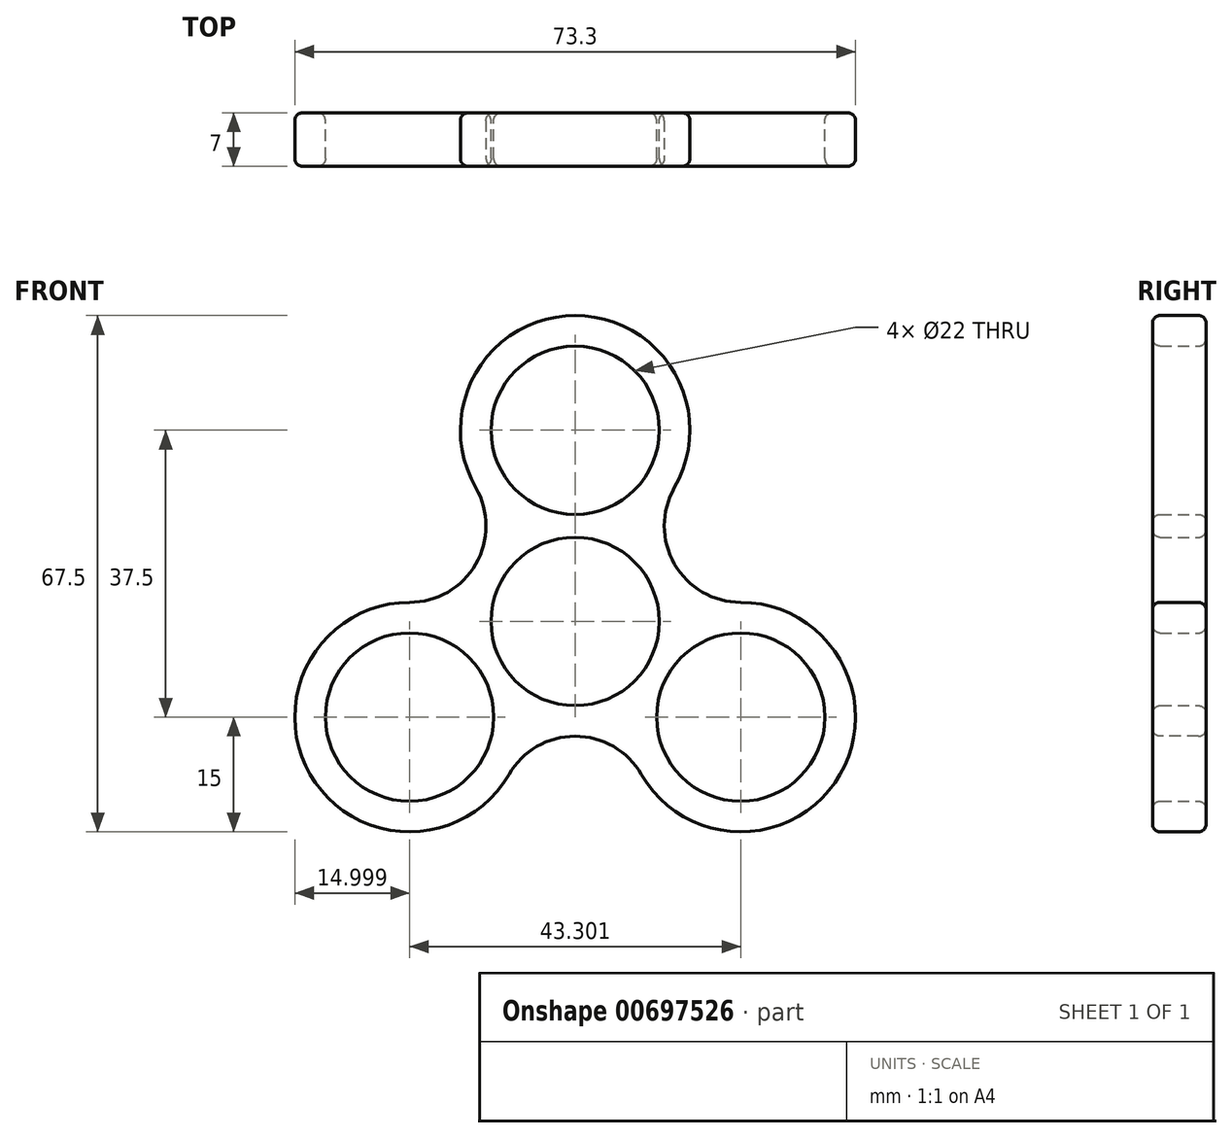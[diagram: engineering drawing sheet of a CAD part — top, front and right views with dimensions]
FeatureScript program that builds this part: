
annotation { "Feature Type Name" : "Feature", "Feature Type Description" : "" }
export const myFeature = defineFeature(function(context is Context, id is Id, definition is map)
    precondition{}
    {
        {
            var Q0;
            Q0=qCreatedBy(makeId("Front.planeOp"),FACE);
            var sketch = newSketch(context, id + "F0", { "sketchPlane" : qUnion([Q0])});
            skCircle(sketch, "E0", {"center": v(0, 0) * mm, "radius": 11 * mm});
            skArc(sketch, "E1", {"start": v(-8.3, 12.5) * mm, "mid": v(-13, 7.5) * mm, "end": v(-14.97, 0.93) * mm});
            skCircle(sketch, "E2", {"center": v(0, 0) * mm, "radius": 36.86 * mm, "construction": true});
            skLineSegment(sketch, "E3", {"start": v(0, 0) * mm, "end": v(31.92, -18.43) * mm, "construction": true});
            skLineSegment(sketch, "E4", {"start": v(0, 0) * mm, "end": v(0, 36.86) * mm, "construction": true});
            skLineSegment(sketch, "E5", {"start": v(0, 0) * mm, "end": v(-31.92, -18.43) * mm, "construction": true});
            skLineSegment(sketch, "E6", {"start": v(0, 0) * mm, "end": v(-13, -7.5) * mm});
            skLineSegment(sketch, "E7", {"start": v(0, 0) * mm, "end": v(-21.65, -12.5) * mm, "construction": true});
            skCircle(sketch, "E8", {"center": v(-21.65, -12.5) * mm, "radius": 11 * mm});
            skArc(sketch, "E9", {"start": v(-14.97, 0.93) * mm, "mid": v(-34.64, -20) * mm, "end": v(-6.68, -13.43) * mm});
            skLineSegment(sketch, "E10", {"start": v(0, 0) * mm, "end": v(0, 25) * mm, "construction": true});
            skCircle(sketch, "E11", {"center": v(0, 25) * mm, "radius": 11 * mm});
            skArc(sketch, "E12", {"start": v(8.3, 12.5) * mm, "mid": v(0, 40) * mm, "end": v(-8.3, 12.5) * mm});
            skLineSegment(sketch, "E13", {"start": v(0, 0) * mm, "end": v(21.65, -12.5) * mm, "construction": true});
            skCircle(sketch, "E14", {"center": v(21.65, -12.5) * mm, "radius": 11 * mm});
            skArc(sketch, "E15", {"start": v(6.68, -13.43) * mm, "mid": v(34.64, -20) * mm, "end": v(14.97, 0.93) * mm});
            skArc(sketch, "E16.trimOffspring", {"start": v(14.97, 0.93) * mm, "mid": v(13, 7.5) * mm, "end": v(8.3, 12.5) * mm});
            skArc(sketch, "E17.trimOffspring", {"start": v(-6.68, -13.43) * mm, "mid": v(0, -15) * mm, "end": v(6.68, -13.43) * mm});
            skSolve(sketch);
        }
        {
            var Q0;
            Q0 = qSketchRegion(id + "F0", true);
            extrude(context, id + "F1", {"entities" : qUnion([Q0]), "depth" : 7 * mm, "offsetDistance" : 25 * mm});
        }
        {
            var Q0;
            Q0=makeQuery(id+"F1.opExtrude","SWEPT_EDGE",EDGE,{"disambiguationData":[OSD([sQuery(id+"F0.wireOp",EDGE,"E9"),sQuery(id+"F0.wireOp",EDGE,"E17.trimOffspring")])]});
            var Q1;
            Q1=makeQuery(id+"F1.opExtrude","SWEPT_EDGE",EDGE,{"disambiguationData":[OSD([sQuery(id+"F0.wireOp",EDGE,"E15"),sQuery(id+"F0.wireOp",EDGE,"E17.trimOffspring")])]});
            var Q2;
            Q2=makeQuery(id+"F1.opExtrude","SWEPT_EDGE",EDGE,{"disambiguationData":[OSD([sQuery(id+"F0.wireOp",EDGE,"E15"),sQuery(id+"F0.wireOp",EDGE,"E16.trimOffspring")])]});
            var Q3;
            Q3=makeQuery(id+"F1.opExtrude","SWEPT_EDGE",EDGE,{"disambiguationData":[OSD([sQuery(id+"F0.wireOp",EDGE,"E12"),sQuery(id+"F0.wireOp",EDGE,"E16.trimOffspring")])]});
            var Q4;
            Q4=makeQuery(id+"F1.opExtrude","SWEPT_EDGE",EDGE,{"disambiguationData":[OSD([sQuery(id+"F0.wireOp",EDGE,"E1"),sQuery(id+"F0.wireOp",EDGE,"E12")])]});
            var Q5;
            Q5=makeQuery(id+"F1.opExtrude","SWEPT_EDGE",EDGE,{"disambiguationData":[OSD([sQuery(id+"F0.wireOp",EDGE,"E1"),sQuery(id+"F0.wireOp",EDGE,"E9")])]});
            fillet(context, id + "F2", {"entities" : qUnion([Q0, Q1, Q2, Q3, Q4, Q5]), "radius" : 10 * mm, "tangentPropagation" : true, "allowEdgeOverflow" : false});
        }
        {
            var Q0;
            Q0=makeQuery(id+"F1.opExtrude","CAP_EDGE",EDGE,{"disambiguationData":[OSD([sQuery(id+"F0.wireOp",EDGE,"E8")])],"isStart":true});
            var Q1;
            Q1=makeQuery(id+"F1.opExtrude","CAP_EDGE",EDGE,{"disambiguationData":[OSD([sQuery(id+"F0.wireOp",EDGE,"E0")])],"isStart":true});
            var Q2;
            {var subQ0=sQuery(id+"F0.wireOp",EDGE,"E12");var subQ1=sQuery(id+"F0.wireOp",EDGE,"E1");Q2=makeQuery(id+"F2.opFillet","BLEND_EDGE",EDGE,{"blendedFrom":[makeQuery(id+"F1.opExtrude","SWEPT_EDGE",EDGE,{"disambiguationData":[OSD([subQ1,subQ0])]}),makeQuery(id+"F1.opExtrude","CAP_FACE",FACE,{"disambiguationData":[OSD([sQuery(id+"F0.wireOp",EDGE,"E0"),subQ1,sQuery(id+"F0.wireOp",EDGE,"E8"),sQuery(id+"F0.wireOp",EDGE,"E9"),sQuery(id+"F0.wireOp",EDGE,"E11"),subQ0,sQuery(id+"F0.wireOp",EDGE,"E14"),sQuery(id+"F0.wireOp",EDGE,"E15"),sQuery(id+"F0.wireOp",EDGE,"E16.trimOffspring"),sQuery(id+"F0.wireOp",EDGE,"E17.trimOffspring")])],"isStart":true})],"blendedInto":[makeQuery(id+"F1.opExtrude","CAP_FACE",FACE,{"disambiguationData":[OSD([sQuery(id+"F0.wireOp",EDGE,"E0"),subQ1,sQuery(id+"F0.wireOp",EDGE,"E8"),sQuery(id+"F0.wireOp",EDGE,"E9"),sQuery(id+"F0.wireOp",EDGE,"E11"),subQ0,sQuery(id+"F0.wireOp",EDGE,"E14"),sQuery(id+"F0.wireOp",EDGE,"E15"),sQuery(id+"F0.wireOp",EDGE,"E16.trimOffspring"),sQuery(id+"F0.wireOp",EDGE,"E17.trimOffspring")])],"isStart":true})]});}
            var Q3;
            Q3=makeQuery(id+"F1.opExtrude","CAP_EDGE",EDGE,{"disambiguationData":[OSD([sQuery(id+"F0.wireOp",EDGE,"E9")])],"isStart":true});
            var Q4;
            Q4=makeQuery(id+"F1.opExtrude","CAP_EDGE",EDGE,{"disambiguationData":[OSD([sQuery(id+"F0.wireOp",EDGE,"E11")])],"isStart":true});
            var Q5;
            Q5=makeQuery(id+"F1.opExtrude","CAP_EDGE",EDGE,{"disambiguationData":[OSD([sQuery(id+"F0.wireOp",EDGE,"E11")])],"isStart":false});
            var Q6;
            Q6=makeQuery(id+"F1.opExtrude","CAP_EDGE",EDGE,{"disambiguationData":[OSD([sQuery(id+"F0.wireOp",EDGE,"E0")])],"isStart":false});
            var Q7;
            Q7=makeQuery(id+"F1.opExtrude","CAP_EDGE",EDGE,{"disambiguationData":[OSD([sQuery(id+"F0.wireOp",EDGE,"E8")])],"isStart":false});
            var Q8;
            Q8=makeQuery(id+"F1.opExtrude","CAP_EDGE",EDGE,{"disambiguationData":[OSD([sQuery(id+"F0.wireOp",EDGE,"E14")])],"isStart":true});
            var Q9;
            Q9=makeQuery(id+"F1.opExtrude","CAP_EDGE",EDGE,{"disambiguationData":[OSD([sQuery(id+"F0.wireOp",EDGE,"E14")])],"isStart":false});
            var Q10;
            Q10=makeQuery(id+"F1.opExtrude","CAP_EDGE",EDGE,{"disambiguationData":[OSD([sQuery(id+"F0.wireOp",EDGE,"E9")])],"isStart":false});
            var Q11;
            {var subQ0=sQuery(id+"F0.wireOp",EDGE,"E12");var subQ1=sQuery(id+"F0.wireOp",EDGE,"E1");Q11=makeQuery(id+"F2.opFillet","BLEND_EDGE",EDGE,{"blendedFrom":[makeQuery(id+"F1.opExtrude","SWEPT_EDGE",EDGE,{"disambiguationData":[OSD([subQ1,subQ0])]}),makeQuery(id+"F1.opExtrude","CAP_FACE",FACE,{"disambiguationData":[OSD([sQuery(id+"F0.wireOp",EDGE,"E0"),subQ1,sQuery(id+"F0.wireOp",EDGE,"E8"),sQuery(id+"F0.wireOp",EDGE,"E9"),sQuery(id+"F0.wireOp",EDGE,"E11"),subQ0,sQuery(id+"F0.wireOp",EDGE,"E14"),sQuery(id+"F0.wireOp",EDGE,"E15"),sQuery(id+"F0.wireOp",EDGE,"E16.trimOffspring"),sQuery(id+"F0.wireOp",EDGE,"E17.trimOffspring")])],"isStart":false})],"blendedInto":[makeQuery(id+"F1.opExtrude","CAP_FACE",FACE,{"disambiguationData":[OSD([sQuery(id+"F0.wireOp",EDGE,"E0"),subQ1,sQuery(id+"F0.wireOp",EDGE,"E8"),sQuery(id+"F0.wireOp",EDGE,"E9"),sQuery(id+"F0.wireOp",EDGE,"E11"),subQ0,sQuery(id+"F0.wireOp",EDGE,"E14"),sQuery(id+"F0.wireOp",EDGE,"E15"),sQuery(id+"F0.wireOp",EDGE,"E16.trimOffspring"),sQuery(id+"F0.wireOp",EDGE,"E17.trimOffspring")])],"isStart":false})]});}
            fillet(context, id + "F3", {"entities" : qUnion([Q0, Q1, Q2, Q3, Q4, Q5, Q6, Q7, Q8, Q9, Q10, Q11]), "radius" : 1 * mm, "tangentPropagation" : true, "allowEdgeOverflow" : false});
        }
    });
